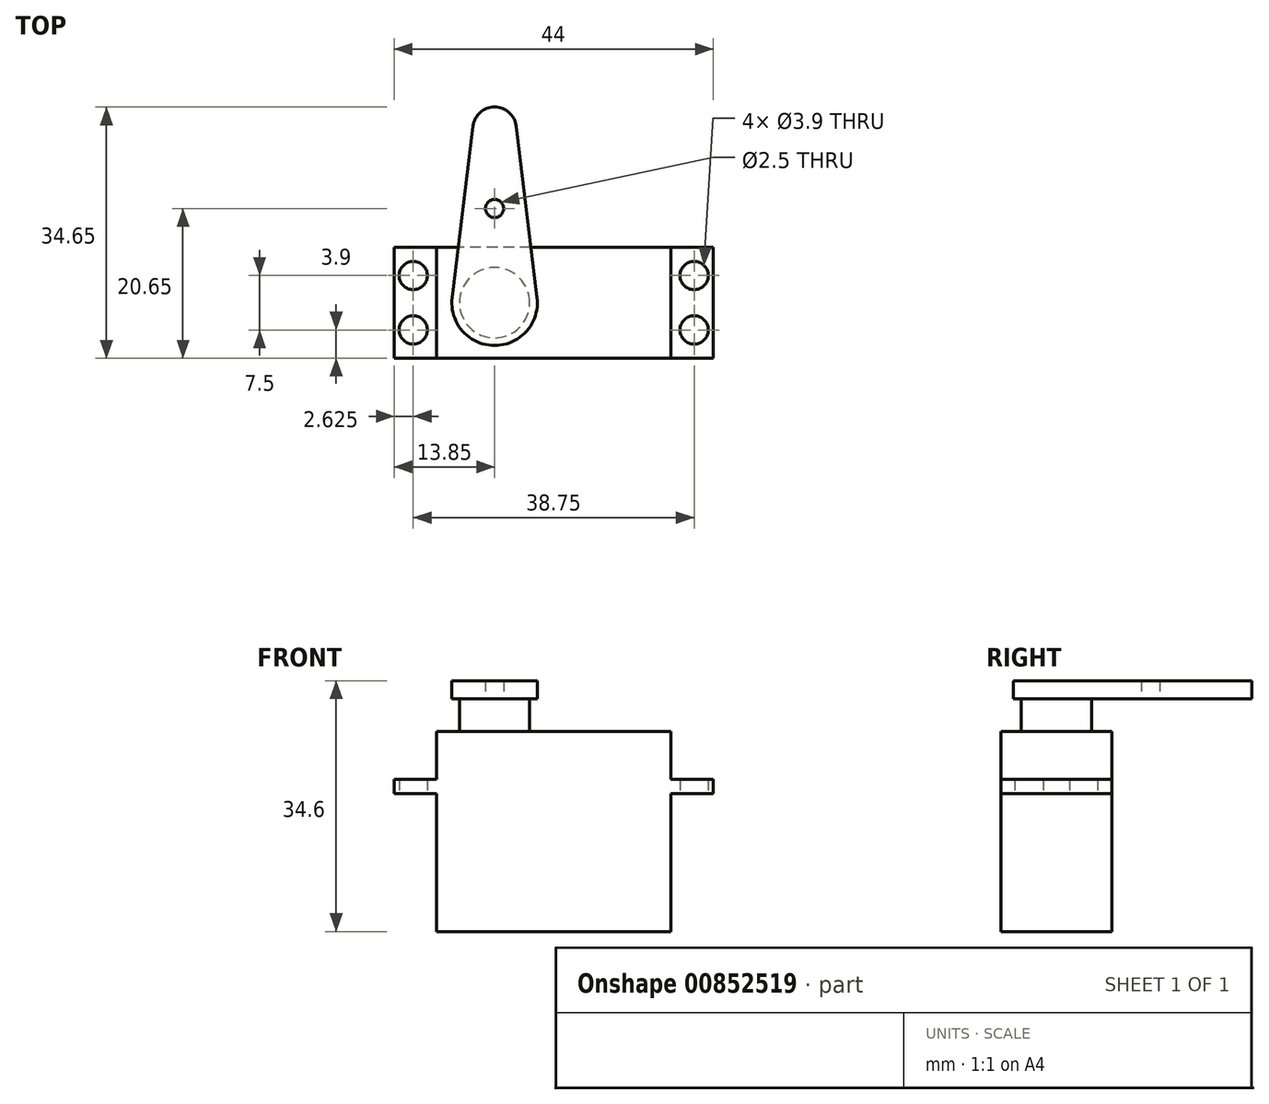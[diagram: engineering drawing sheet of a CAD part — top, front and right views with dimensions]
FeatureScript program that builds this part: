
annotation { "Feature Type Name" : "Feature", "Feature Type Description" : "" }
export const myFeature = defineFeature(function(context is Context, id is Id, definition is map)
    precondition{}
    {
        {
            var Q0;
            Q0=qCreatedBy(makeId("Top.planeOp"),FACE);
            var sketch = newSketch(context, id + "F0", { "sketchPlane" : qUnion([Q0])});
            skLineSegment(sketch, "E0.bottom", {"start": v(16.15, 7.65) * mm, "end": v(-16.15, 7.65) * mm});
            skLineSegment(sketch, "E0.top", {"start": v(16.15, -7.65) * mm, "end": v(-16.15, -7.65) * mm});
            skLineSegment(sketch, "E0.left", {"start": v(16.15, 7.65) * mm, "end": v(16.15, -7.65) * mm});
            skLineSegment(sketch, "E0.right", {"start": v(-16.15, 7.65) * mm, "end": v(-16.15, -7.65) * mm});
            skPoint(sketch, "E0.middle", {"position": v(0, 0) * mm});
            skSolve(sketch);
        }
        {
            var Q0;
            Q0=makeQuery(id+"F0.imprint","IMPRINT",FACE,{"disambiguationData":[TD([[makeQuery(id+"F0.imprint","IMPRINT",EDGE,{"derivedFrom":sQuery(id+"F0.wireOp",EDGE,"E0.bottom")}),1.0]])]});
            extrude(context, id + "F1", {"entities" : qUnion([Q0]), "depth" : 27.6 * mm, "offsetDistance" : 25 * mm});
        }
        {
            var Q0;
            Q0=qCreatedBy(makeId("Top.planeOp"),FACE);
            cPlane(context, id + "F2", {"entities" : qUnion([Q0]), "cplaneType" : CPlaneType.OFFSET, "offset" : 19 * mm, "width" : 150 * mm, "height" : 150 * mm});
        }
        {
            var Q0;
            Q0=qCreatedBy(id+"F2.planeOp",FACE);
            var sketch = newSketch(context, id + "F3", { "sketchPlane" : qUnion([Q0])});
            skLineSegment(sketch, "E1.0.0", {"start": v(-16.15, -7.65) * mm, "end": v(16.15, -7.65) * mm, "construction": true});
            skLineSegment(sketch, "E1.0.1", {"start": v(16.15, -7.65) * mm, "end": v(16.15, 7.65) * mm, "construction": true});
            skLineSegment(sketch, "E1.0.2", {"start": v(16.15, 7.65) * mm, "end": v(-16.15, 7.65) * mm, "construction": true});
            skLineSegment(sketch, "E1.0.3", {"start": v(-16.15, 7.65) * mm, "end": v(-16.15, -7.65) * mm, "construction": true});
            skLineSegment(sketch, "E2.bottom", {"start": v(22, 7.65) * mm, "end": v(-22, 7.65) * mm});
            skLineSegment(sketch, "E2.top", {"start": v(22, -7.65) * mm, "end": v(-22, -7.65) * mm});
            skLineSegment(sketch, "E2.left", {"start": v(22, 7.65) * mm, "end": v(22, -7.65) * mm});
            skLineSegment(sketch, "E2.right", {"start": v(-22, 7.65) * mm, "end": v(-22, -7.65) * mm});
            skPoint(sketch, "E2.middle", {"position": v(0, 0) * mm});
            skLineSegment(sketch, "E3.bottom", {"start": v(-19.38, 3.75) * mm, "end": v(19.38, 3.75) * mm, "construction": true});
            skLineSegment(sketch, "E3.top", {"start": v(-19.38, -3.75) * mm, "end": v(19.38, -3.75) * mm, "construction": true});
            skLineSegment(sketch, "E3.left", {"start": v(-19.38, 3.75) * mm, "end": v(-19.38, -3.75) * mm, "construction": true});
            skLineSegment(sketch, "E3.right", {"start": v(19.38, 3.75) * mm, "end": v(19.38, -3.75) * mm, "construction": true});
            skCircle(sketch, "E4", {"center": v(-19.38, 3.75) * mm, "radius": 1.95 * mm});
            skCircle(sketch, "E5", {"center": v(19.38, 3.75) * mm, "radius": 1.95 * mm});
            skCircle(sketch, "E6", {"center": v(19.38, -3.75) * mm, "radius": 1.95 * mm});
            skCircle(sketch, "E7", {"center": v(-19.38, -3.75) * mm, "radius": 1.95 * mm});
            skSolve(sketch);
        }
        {
            var Q0;
            Q0=makeQuery(id+"F3.imprint","IMPRINT",FACE,{"disambiguationData":[TD([[makeQuery(id+"F3.imprint","IMPRINT",EDGE,{"derivedFrom":sQuery(id+"F3.wireOp",EDGE,"E2.bottom")}),1.0]])]});
            extrude(context, id + "F4", {"entities" : qUnion([Q0]), "operationType" : NewBodyOperationType.ADD, "depth" : 2 * mm, "offsetDistance" : 25 * mm});
        }
        {
            var Q0;
            Q0=makeQuery(id+"F1.opExtrude","CAP_FACE",FACE,{"disambiguationData":[OSD([sQuery(id+"F0.wireOp",EDGE,"E0.bottom"),sQuery(id+"F0.wireOp",EDGE,"E0.top"),sQuery(id+"F0.wireOp",EDGE,"E0.left"),sQuery(id+"F0.wireOp",EDGE,"E0.right")])],"isStart":false});
            var sketch = newSketch(context, id + "F5", { "sketchPlane" : qUnion([Q0])});
            skCircle(sketch, "E8", {"center": v(-8.15, 0) * mm, "radius": 4.85 * mm});
            skLineSegment(sketch, "E9.0", {"start": v(-16.15, 7.65) * mm, "end": v(-16.15, -7.65) * mm, "construction": true});
            skSolve(sketch);
        }
        {
            var Q0;
            Q0=makeQuery(id+"F5.imprint","IMPRINT",FACE,{"disambiguationData":[TD([[makeQuery(id+"F5.imprint","IMPRINT",EDGE,{"derivedFrom":sQuery(id+"F5.wireOp",EDGE,"E8")}),1.0]])]});
            extrude(context, id + "F6", {"entities" : qUnion([Q0]), "operationType" : NewBodyOperationType.ADD, "depth" : 4.5 * mm, "offsetDistance" : 25 * mm});
        }
        {
            var Q0;
            Q0=makeQuery(id+"F6.opExtrude","CAP_FACE",FACE,{"disambiguationData":[OSD([sQuery(id+"F5.wireOp",EDGE,"E8")])],"isStart":false});
            var sketch = newSketch(context, id + "F7", { "sketchPlane" : qUnion([Q0])});
            skCircle(sketch, "E10.0", {"center": v(-8.15, 0) * mm, "radius": 4.85 * mm, "construction": true});
            skLineSegment(sketch, "E11", {"start": v(-8.15, 0) * mm, "end": v(-8.15, 24) * mm, "construction": true});
            skCircle(sketch, "E12", {"center": v(-8.15, 0) * mm, "radius": 5.9 * mm});
            skCircle(sketch, "E13", {"center": v(-8.15, 24) * mm, "radius": 3 * mm});
            skLineSegment(sketch, "E14", {"start": v(-14, 0.71) * mm, "end": v(-11.13, 24.36) * mm});
            skLineSegment(sketch, "E15", {"start": v(-2.3, 0.71) * mm, "end": v(-5.17, 24.36) * mm});
            skLineSegment(sketch, "E16", {"start": v(-8.15, 0) * mm, "end": v(-8.15, 13) * mm, "construction": true});
            skCircle(sketch, "E17", {"center": v(-8.15, 13) * mm, "radius": 1.25 * mm});
            skSolve(sketch);
        }
        {
            var Q0;
            Q0 = qSketchRegion(id + "F7", true);
            extrude(context, id + "F8", {"entities" : qUnion([Q0]), "operationType" : NewBodyOperationType.ADD, "depth" : 2.5 * mm, "offsetDistance" : 25 * mm});
        }
    });
